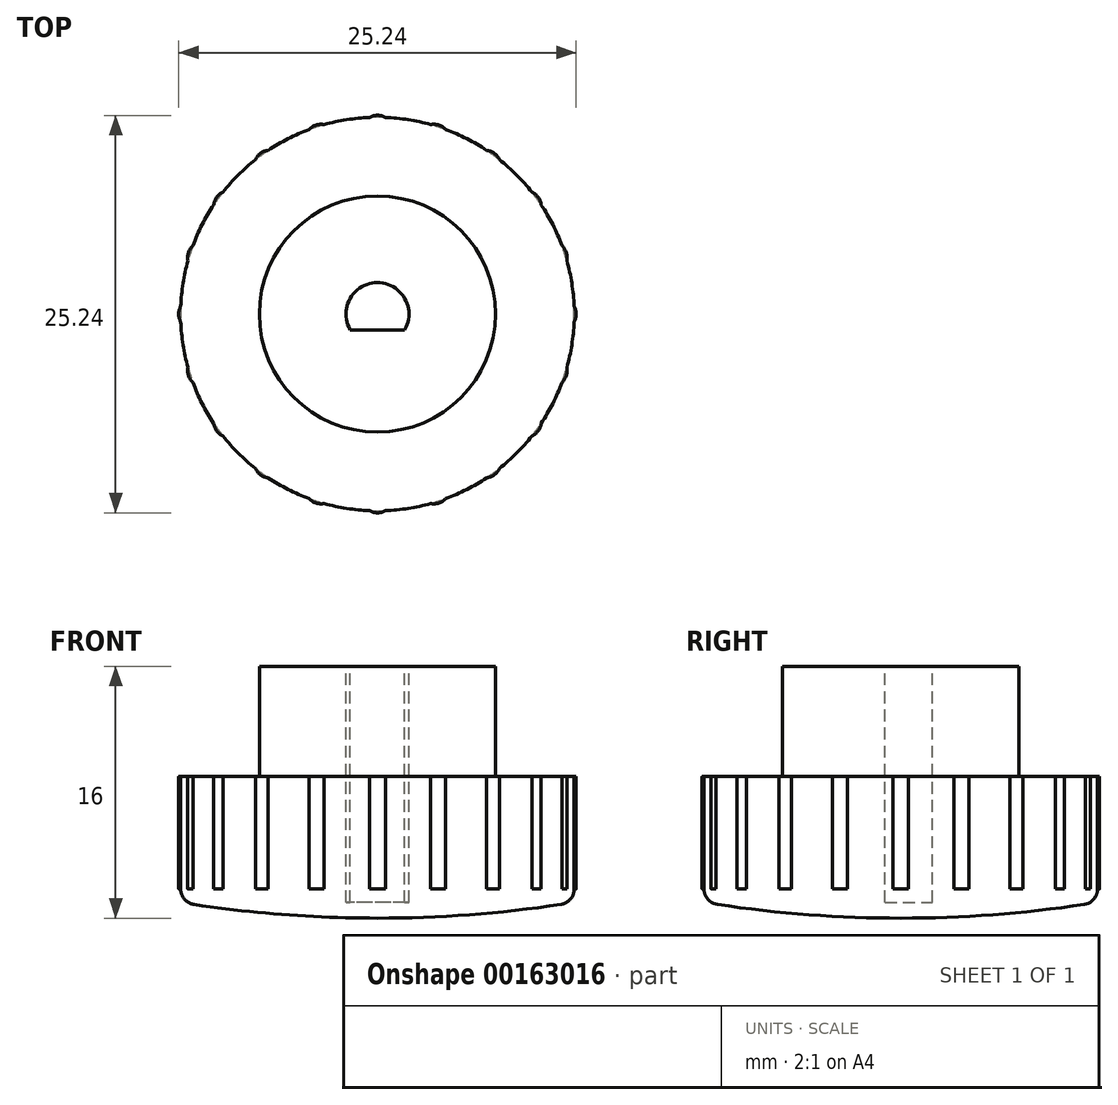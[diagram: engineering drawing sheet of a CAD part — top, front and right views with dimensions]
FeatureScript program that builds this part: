
annotation { "Feature Type Name" : "Feature", "Feature Type Description" : "" }
export const myFeature = defineFeature(function(context is Context, id is Id, definition is map)
    precondition{}
    {
        {
            var Q0;
            Q0=qCreatedBy(makeId("Top.planeOp"),FACE);
            var sketch = newSketch(context, id + "F0", { "sketchPlane" : qUnion([Q0])});
            skCircle(sketch, "E0", {"center": v(0, 0) * mm, "radius": 7.5 * mm});
            skSolve(sketch);
        }
        {
            var Q0;
            Q0=makeQuery(id+"F0.imprint","IMPRINT",FACE,{"disambiguationData":[TD([[makeQuery(id+"F0.imprint","IMPRINT",EDGE,{"derivedFrom":sQuery(id+"F0.wireOp",EDGE,"E0")}),1.0]])]});
            extrude(context, id + "F1", {"entities" : qUnion([Q0]), "depth" : 7 * mm});
        }
        {
            var Q0;
            Q0=qCreatedBy(makeId("Front.planeOp"),FACE);
            var sketch = newSketch(context, id + "F2", { "sketchPlane" : qUnion([Q0])});
            skLineSegment(sketch, "E1", {"start": v(0, -9) * mm, "end": v(0, 0) * mm});
            skLineSegment(sketch, "E2", {"start": v(0, 0) * mm, "end": v(-12.5, 0) * mm});
            skLineSegment(sketch, "E3", {"start": v(-12.5, 0) * mm, "end": v(-12.5, -8) * mm});
            skLineSegment(sketch, "E4", {"start": v(0, -9) * mm, "end": v(3.53, -9) * mm, "construction": true});
            skArc(sketch, "E5", {"start": v(0, -9) * mm, "mid": v(-6.27, -8.75) * mm, "end": v(-12.5, -8) * mm});
            skSolve(sketch);
        }
        {
            var Q0;
            Q0=makeQuery(id+"F2.imprint","IMPRINT",FACE,{"disambiguationData":[TD([[makeQuery(id+"F2.imprint","IMPRINT",EDGE,{"derivedFrom":sQuery(id+"F2.wireOp",EDGE,"E1")}),1.0]])]});
            var Q1;
            Q1=sQuery(id+"F2.wireOp",EDGE,"E1");
            revolve(context, id + "F3", {"operationType" : NewBodyOperationType.ADD, "entities" : qUnion([Q0]), "axis" : qUnion([Q1]), "revolveType" : RevolveType.FULL});
        }
        {
            var Q0;
            Q0=qCreatedBy(makeId("Front.planeOp"),FACE);
            var sketch = newSketch(context, id + "F4", { "sketchPlane" : qUnion([Q0])});
            skArc(sketch, "E6", {"start": v(12.5, 0) * mm, "mid": v(11.96, -4) * mm, "end": v(12.5, -8) * mm});
            skLineSegment(sketch, "E7", {"start": v(12.5, 0) * mm, "end": v(12.5, -8) * mm});
            skSolve(sketch);
        }
        {
            var Q0;
            Q0=makeQuery(id+"F3.opRevolve","SWEPT_FACE",FACE,{"disambiguationData":[OSD([sQuery(id+"F2.wireOp",EDGE,"E2")])]});
            var sketch = newSketch(context, id + "F5", { "sketchPlane" : qUnion([Q0])});
            skArc(sketch, "E8", {"start": v(-0.5, -12.49) * mm, "mid": v(0, -12.62) * mm, "end": v(0.5, -12.49) * mm});
            skLineSegment(sketch, "E9", {"start": v(0.5, -12.49) * mm, "end": v(-0.5, -12.49) * mm});
            skSolve(sketch);
        }
        {
            var Q0;
            Q0=makeQuery(id+"F3.opRevolve","SWEPT_EDGE",EDGE,{"disambiguationData":[OSD([sQuery(id+"F2.wireOp",EDGE,"E3"),sQuery(id+"F2.wireOp",EDGE,"E5")])]});
            fillet(context, id + "F6", {"entities" : qUnion([Q0]), "radius" : 1 * mm, "tangentPropagation" : true, "allowEdgeOverflow" : false});
        }
        {
            var Q0;
            {var subQ0=sQuery(id+"F5.wireOp",EDGE,"E8");Q0=makeQuery(id+"F5.imprint","IMPRINT",FACE,{"disambiguationData":[TD([[makeQuery(id+"F5.imprint","IMPRINT",EDGE,{"derivedFrom":subQ0}),1.0]])]});}
            extrude(context, id + "F7", {"entities" : qUnion([Q0]), "oppositeDirection" : true, "depth" : 7.15 * mm});
        }
        {
            var Q0;
            Q0=qCreatedBy(makeId("Front.planeOp"),FACE);
            var sketch = newSketch(context, id + "F8", { "sketchPlane" : qUnion([Q0])});
            skLineSegment(sketch, "E10", {"start": v(0, 0) * mm, "end": v(0, -17.44) * mm});
            skSolve(sketch);
        }
        {
            var Q0;
            Q0=makeQuery(id+"F7.opExtrude","SWEPT_BODY",BODY,{"disambiguationData":[OSD([sQuery(id+"F2.wireOp",EDGE,"E2"),sQuery(id+"F2.wireOp",EDGE,"E3"),sQuery(id+"F5.wireOp",EDGE,"E8")])]});
            var Q1;
            Q1=sQuery(id+"F8.wireOp",EDGE,"E10");
            circularPattern(context, id + "F9", {"operationType" : NewBodyOperationType.ADD, "entities" : qUnion([Q0]), "axis" : qUnion([Q1]), "angle" : 360 * degree, "instanceCount" : 20, "equalSpace" : true});
        }
        {
            var Q0;
            Q0=makeQuery(id+"F1.opExtrude","CAP_FACE",FACE,{"disambiguationData":[OSD([sQuery(id+"F0.wireOp",EDGE,"E0")])],"isStart":false});
            var sketch = newSketch(context, id + "F10", { "sketchPlane" : qUnion([Q0])});
            skArc(sketch, "E11", {"start": v(1.73, -1) * mm, "mid": v(0, 2) * mm, "end": v(-1.73, -1) * mm});
            skLineSegment(sketch, "E12", {"start": v(1.73, -1) * mm, "end": v(-1.73, -1) * mm});
            skSolve(sketch);
        }
        {
            var Q0;
            Q0=makeQuery(id+"F10.imprint","IMPRINT",FACE,{"disambiguationData":[TD([[makeQuery(id+"F10.imprint","IMPRINT",EDGE,{"derivedFrom":sQuery(id+"F10.wireOp",EDGE,"E11")}),1.0]])]});
            extrude(context, id + "F11", {"entities" : qUnion([Q0]), "operationType" : NewBodyOperationType.REMOVE, "oppositeDirection" : true, "depth" : 15 * mm});
        }
    });
